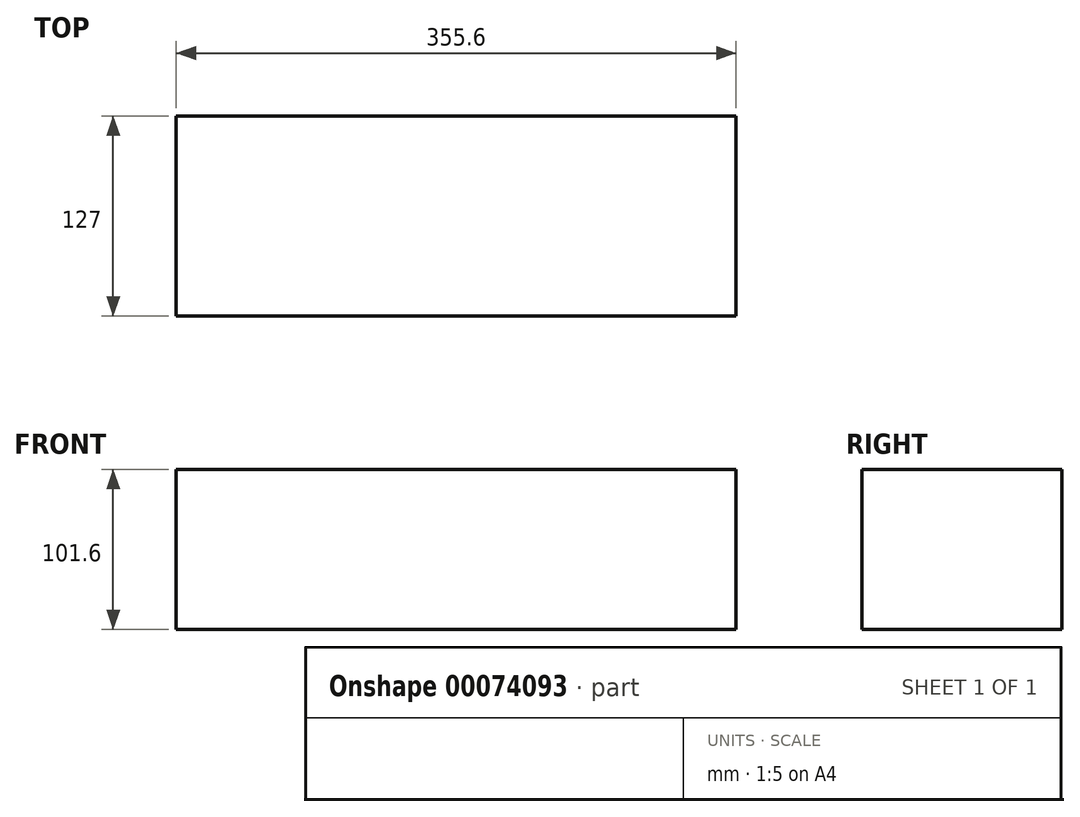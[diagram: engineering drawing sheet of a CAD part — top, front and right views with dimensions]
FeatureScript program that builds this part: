
annotation { "Feature Type Name" : "Feature", "Feature Type Description" : "" }
export const myFeature = defineFeature(function(context is Context, id is Id, definition is map)
    precondition{}
    {
        {
            var Q0;
            Q0=qCreatedBy(makeId("Top.planeOp"),FACE);
            var sketch = newSketch(context, id + "F0", { "sketchPlane" : qUnion([Q0])});
            skLineSegment(sketch, "E0.rect.bottom", {"start": v(177.8, -63.5) * mm, "end": v(-177.8, -63.5) * mm});
            skLineSegment(sketch, "E0.rect.top", {"start": v(177.8, 63.5) * mm, "end": v(-177.8, 63.5) * mm});
            skLineSegment(sketch, "E0.rect.left", {"start": v(177.8, -63.5) * mm, "end": v(177.8, 63.5) * mm});
            skLineSegment(sketch, "E0.rect.right", {"start": v(-177.8, -63.5) * mm, "end": v(-177.8, 63.5) * mm});
            skPoint(sketch, "E0.rect.middle", {"position": v(0, 0) * mm});
            skSolve(sketch);
        }
        {
            var Q0;
            Q0=qSketchRegion(id+"F0",true);
            extrude(context, id + "F1", {"entities" : qUnion([Q0]), "depth" : 101.6 * mm});
        }
    });
